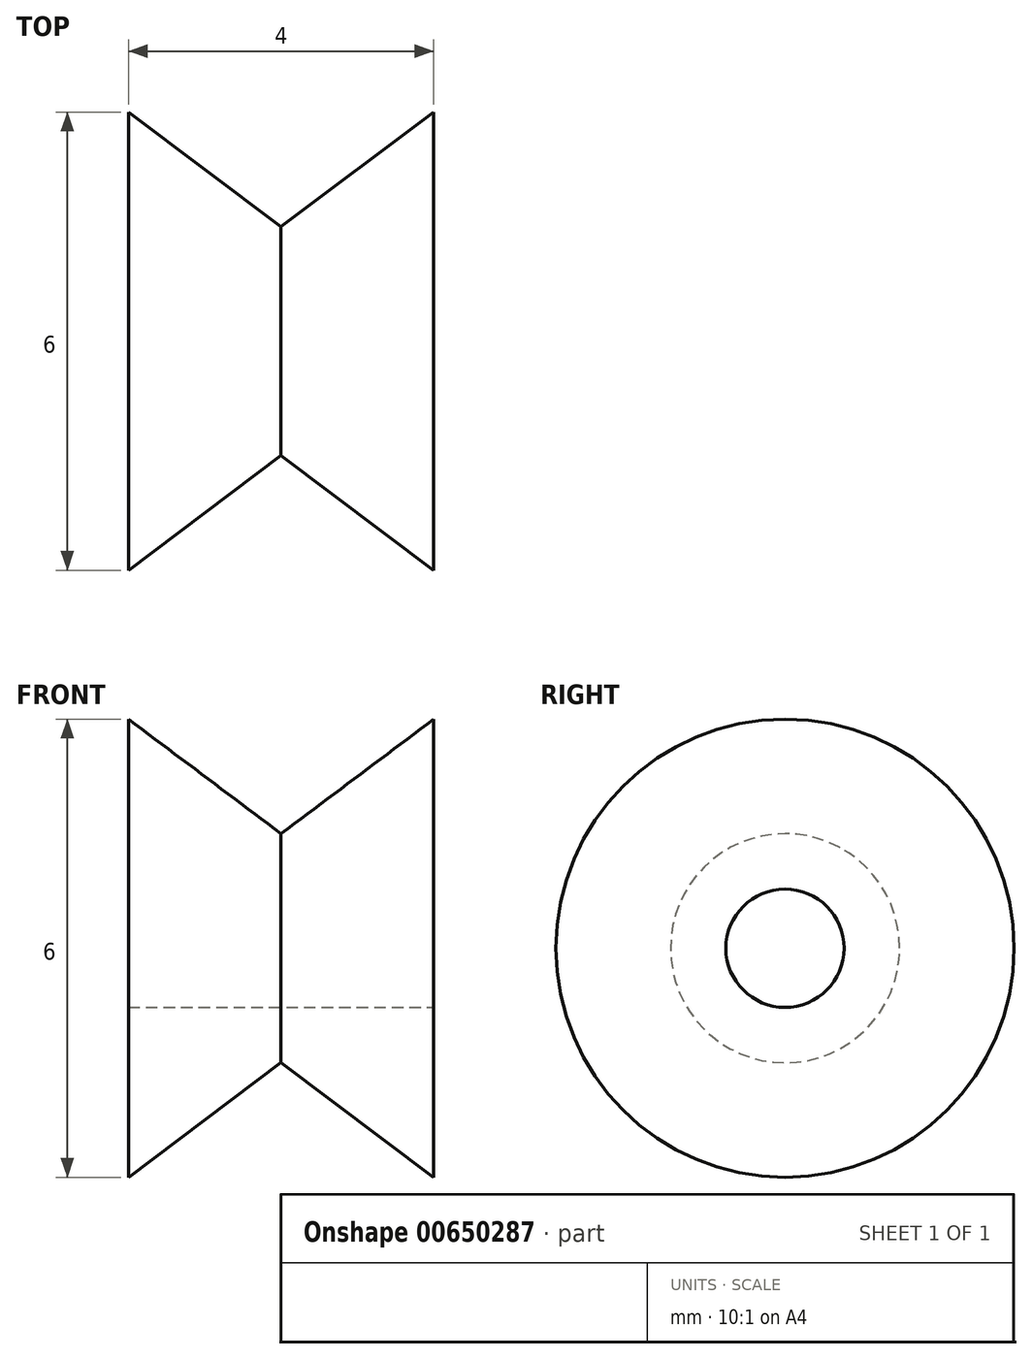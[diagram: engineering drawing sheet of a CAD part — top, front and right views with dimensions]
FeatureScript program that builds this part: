
annotation { "Feature Type Name" : "Feature", "Feature Type Description" : "" }
export const myFeature = defineFeature(function(context is Context, id is Id, definition is map)
    precondition{}
    {
        {
            var Q0;
            Q0=qCreatedBy(makeId("Front.planeOp"),FACE);
            var sketch = newSketch(context, id + "F0", { "sketchPlane" : qUnion([Q0])});
            skLineSegment(sketch, "E0", {"start": v(2, 0) * mm, "end": v(2, 3) * mm});
            skLineSegment(sketch, "E1", {"start": v(2, 3) * mm, "end": v(0, 1.5) * mm});
            skLineSegment(sketch, "E2", {"start": v(0, 1.5) * mm, "end": v(-2, 3) * mm});
            skLineSegment(sketch, "E3", {"start": v(-2, 3) * mm, "end": v(-2, 0) * mm});
            skLineSegment(sketch, "E4", {"start": v(-2, 0) * mm, "end": v(2, 0) * mm});
            skSolve(sketch);
        }
        {
            var Q0;
            Q0=makeQuery(id+"F0.imprint","IMPRINT",FACE,{"disambiguationData":[TD([[makeQuery(id+"F0.imprint","IMPRINT",EDGE,{"derivedFrom":sQuery(id+"F0.wireOp",EDGE,"E0")}),1.0]])]});
            var Q1;
            Q1=sQuery(id+"F0.wireOp",EDGE,"E4");
            revolve(context, id + "F1", {"entities" : qUnion([Q0]), "axis" : qUnion([Q1]), "revolveType" : RevolveType.FULL});
        }
        {
            var Q0;
            Q0=makeQuery(id+"F1.opRevolve","SWEPT_FACE",FACE,{"disambiguationData":[OSD([sQuery(id+"F0.wireOp",EDGE,"E0")])]});
            var sketch = newSketch(context, id + "F2", { "sketchPlane" : qUnion([Q0])});
            skCircle(sketch, "E5", {"center": v(0, 0) * mm, "radius": 0.78 * mm});
            skSolve(sketch);
        }
        {
            var Q0;
            Q0 = qSketchRegion(id + "F2", true);
            extrude(context, id + "F3", {"entities" : qUnion([Q0]), "operationType" : NewBodyOperationType.REMOVE, "oppositeDirection" : true, "depth" : 25 * mm, "offsetDistance" : 25 * mm});
        }
    });
